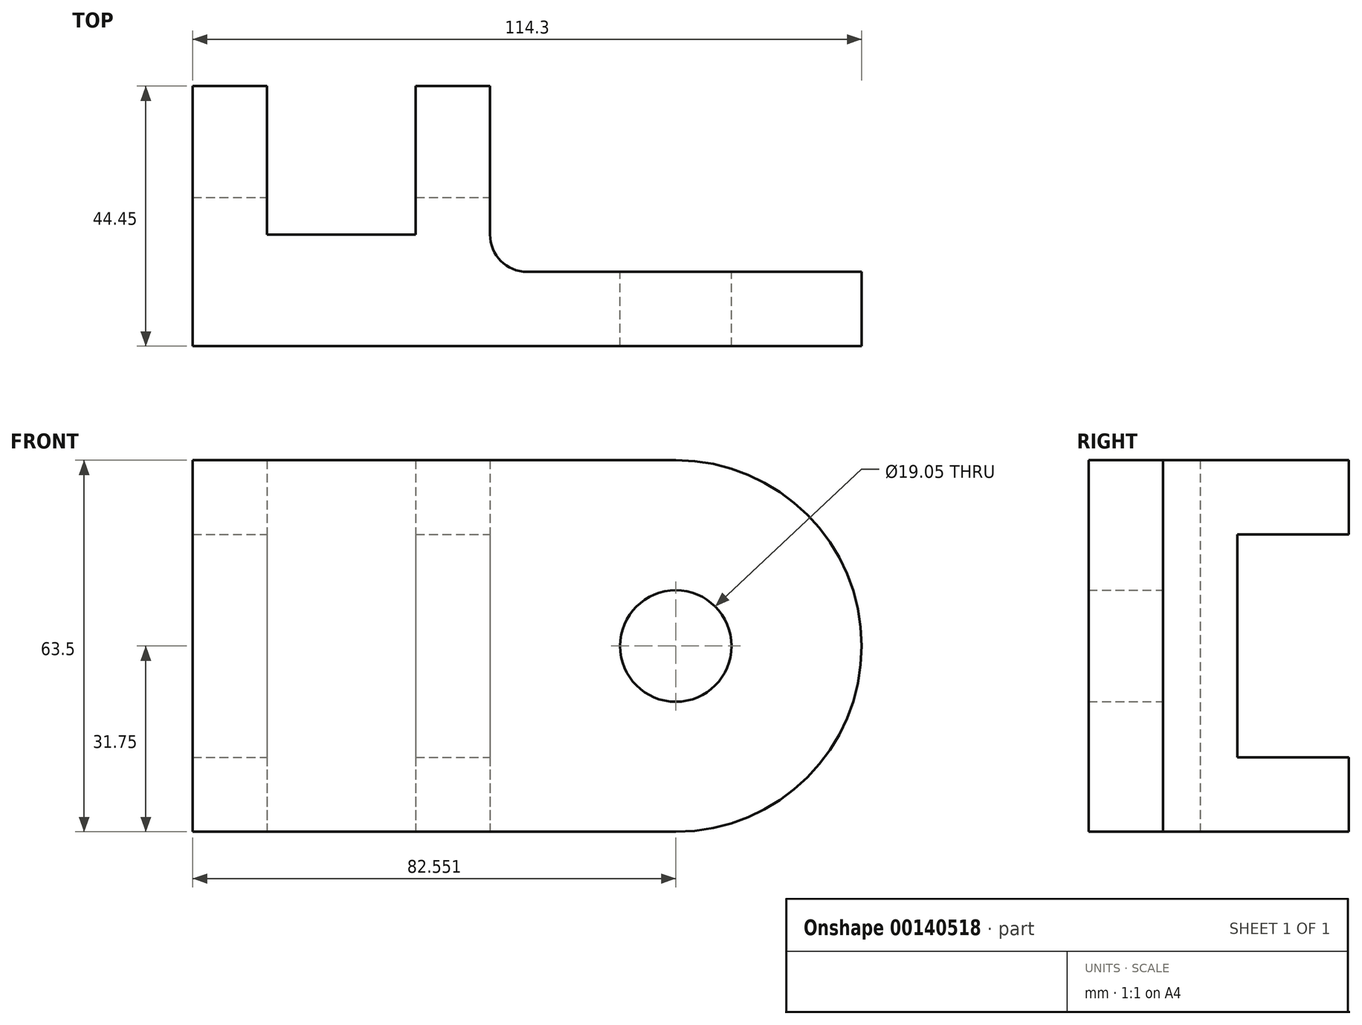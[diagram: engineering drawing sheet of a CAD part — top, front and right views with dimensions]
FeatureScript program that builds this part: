
annotation { "Feature Type Name" : "Feature", "Feature Type Description" : "" }
export const myFeature = defineFeature(function(context is Context, id is Id, definition is map)
    precondition{}
    {
        {
            var Q0;
            Q0=qCreatedBy(makeId("Top.planeOp"),FACE);
            var sketch = newSketch(context, id + "F0", { "sketchPlane" : qUnion([Q0])});
            skLineSegment(sketch, "E0", {"start": v(-38, 20.16) * mm, "end": v(-38, -24.29) * mm});
            skLineSegment(sketch, "E1", {"start": v(-38, -24.29) * mm, "end": v(44.55, -24.29) * mm});
            skLineSegment(sketch, "E2", {"start": v(44.55, -24.29) * mm, "end": v(44.55, -11.59) * mm});
            skLineSegment(sketch, "E3", {"start": v(44.55, -11.59) * mm, "end": v(12.8, -11.59) * mm});
            skLineSegment(sketch, "E4", {"start": v(12.8, -11.59) * mm, "end": v(12.8, 20.16) * mm});
            skLineSegment(sketch, "E5", {"start": v(12.8, 20.16) * mm, "end": v(0.1, 20.16) * mm});
            skLineSegment(sketch, "E6", {"start": v(0.1, 20.16) * mm, "end": v(0.1, -5.24) * mm});
            skLineSegment(sketch, "E7", {"start": v(0.1, -5.24) * mm, "end": v(-25.3, -5.24) * mm});
            skLineSegment(sketch, "E8", {"start": v(-25.3, -5.24) * mm, "end": v(-25.3, 20.16) * mm});
            skLineSegment(sketch, "E9", {"start": v(-25.3, 20.16) * mm, "end": v(-38, 20.16) * mm});
            skSolve(sketch);
        }
        {
            var Q0;
            Q0=makeQuery(id+"F0.imprint","IMPRINT",FACE,{"disambiguationData":[TD([[makeQuery(id+"F0.imprint","IMPRINT",EDGE,{"derivedFrom":sQuery(id+"F0.wireOp",EDGE,"E0")}),1.0]])]});
            extrude(context, id + "F1", {"entities" : qUnion([Q0]), "depth" : 63.5 * mm});
        }
        {
            var Q0;
            Q0=makeQuery(id+"F1.opExtrude","SWEPT_FACE",FACE,{"disambiguationData":[OSD([sQuery(id+"F0.wireOp",EDGE,"E1")])]});
            var sketch = newSketch(context, id + "F2", { "sketchPlane" : qUnion([Q0])});
            skCircle(sketch, "E10", {"center": v(44.55, 31.75) * mm, "radius": 31.75 * mm});
            skSolve(sketch);
        }
        {
            var Q0;
            {var subQ1=sQuery(id+"F0.wireOp",EDGE,"E1");var subQ2=makeQuery(id+"F1.opExtrude","SWEPT_EDGE",EDGE,{"disambiguationData":[OSD([subQ1,sQuery(id+"F0.wireOp",EDGE,"E2")])]});Q0=makeQuery(id+"F2.imprint","IMPRINT",FACE,{"disambiguationData":[TD([[makeQuery(id+"F2.imprint","IMPRINT",EDGE,{"derivedFrom":subQ2}),1.0]])]});}
            var Q1;
            {var subQ1=sQuery(id+"F0.wireOp",EDGE,"E1");var subQ2=makeQuery(id+"F1.opExtrude","SWEPT_EDGE",EDGE,{"disambiguationData":[OSD([subQ1,sQuery(id+"F0.wireOp",EDGE,"E2")])]});Q1=makeQuery(id+"F2.imprint","IMPRINT",FACE,{"disambiguationData":[TD([[makeQuery(id+"F2.imprint","IMPRINT",EDGE,{"derivedFrom":subQ2}),-1.0]])]});}
            extrude(context, id + "F3", {"entities" : qUnion([Q0, Q1]), "operationType" : NewBodyOperationType.ADD, "oppositeDirection" : true, "depth" : 12.7 * mm});
        }
        {
            var Q0;
            Q0=makeQuery(id+"F3.boolean.opBoolean","MERGE",FACE,{"derivedFrom":[makeQuery(id+"F1.opExtrude","SWEPT_FACE",FACE,{"disambiguationData":[OSD([sQuery(id+"F0.wireOp",EDGE,"E3")])]}),makeQuery(id+"F3.opExtrude","CAP_FACE",FACE,{"disambiguationData":[OSD([sQuery(id+"F2.wireOp",EDGE,"E10")])],"isStart":false})]});
            var sketch = newSketch(context, id + "F4", { "sketchPlane" : qUnion([Q0])});
            skCircle(sketch, "E11", {"center": v(-44.55, 31.75) * mm, "radius": 9.53 * mm});
            skSolve(sketch);
        }
        {
            var Q0;
            Q0=makeQuery(id+"F4.imprint","IMPRINT",FACE,{"disambiguationData":[TD([[makeQuery(id+"F4.imprint","IMPRINT",EDGE,{"derivedFrom":sQuery(id+"F4.wireOp",EDGE,"E11")}),1.0]])]});
            extrude(context, id + "F5", {"entities" : qUnion([Q0]), "operationType" : NewBodyOperationType.REMOVE, "oppositeDirection" : true, "depth" : 25.4 * mm});
        }
        {
            var Q0;
            Q0=makeQuery(id+"F1.opExtrude","SWEPT_FACE",FACE,{"disambiguationData":[OSD([sQuery(id+"F0.wireOp",EDGE,"E4")])]});
            var sketch = newSketch(context, id + "F6", { "sketchPlane" : qUnion([Q0])});
            skLineSegment(sketch, "E12", {"start": v(20.16, 50.8) * mm, "end": v(1.11, 50.8) * mm});
            skLineSegment(sketch, "E13", {"start": v(1.11, 50.8) * mm, "end": v(1.11, 12.7) * mm});
            skLineSegment(sketch, "E14", {"start": v(1.11, 12.7) * mm, "end": v(20.16, 12.7) * mm});
            skSolve(sketch);
        }
        {
            var Q0;
            Q0 = qSketchRegion(id + "F6", true);
            var Q1;
            {var subQ0=sQuery(id+"F6.wireOp",EDGE,"E12");Q1=makeQuery(id+"F6.imprint","IMPRINT",FACE,{"disambiguationData":[TD([[makeQuery(id+"F6.imprint","IMPRINT",EDGE,{"derivedFrom":subQ0}),1.0]])]});}
            extrude(context, id + "F7", {"entities" : qUnion([Q0, Q1]), "operationType" : NewBodyOperationType.REMOVE, "oppositeDirection" : true, "depth" : 25.4 * mm});
        }
        {
            var Q0;
            Q0=makeQuery(id+"F1.opExtrude","SWEPT_FACE",FACE,{"disambiguationData":[OSD([sQuery(id+"F0.wireOp",EDGE,"E8")])]});
            var sketch = newSketch(context, id + "F8", { "sketchPlane" : qUnion([Q0])});
            skLineSegment(sketch, "E15", {"start": v(20.16, 50.8) * mm, "end": v(1.11, 50.8) * mm});
            skLineSegment(sketch, "E16", {"start": v(1.11, 50.8) * mm, "end": v(1.11, 12.7) * mm});
            skLineSegment(sketch, "E17", {"start": v(1.11, 12.7) * mm, "end": v(20.16, 12.7) * mm});
            skSolve(sketch);
        }
        {
            var Q0;
            Q0 = qSketchRegion(id + "F8", true);
            var Q1;
            {var subQ0=sQuery(id+"F8.wireOp",EDGE,"E15");Q1=makeQuery(id+"F8.imprint","IMPRINT",FACE,{"disambiguationData":[TD([[makeQuery(id+"F8.imprint","IMPRINT",EDGE,{"derivedFrom":subQ0}),1.0]])]});}
            extrude(context, id + "F9", {"entities" : qUnion([Q0, Q1]), "operationType" : NewBodyOperationType.REMOVE, "oppositeDirection" : true, "depth" : 25.4 * mm});
        }
        {
            var Q0;
            Q0=makeQuery(id+"F1.opExtrude","SWEPT_EDGE",EDGE,{"disambiguationData":[OSD([sQuery(id+"F0.wireOp",EDGE,"E3"),sQuery(id+"F0.wireOp",EDGE,"E4")])]});
            fillet(context, id + "F10", {"entities" : qUnion([Q0]), "radius" : 6.35 * mm, "tangentPropagation" : true, "allowEdgeOverflow" : false});
        }
    });
